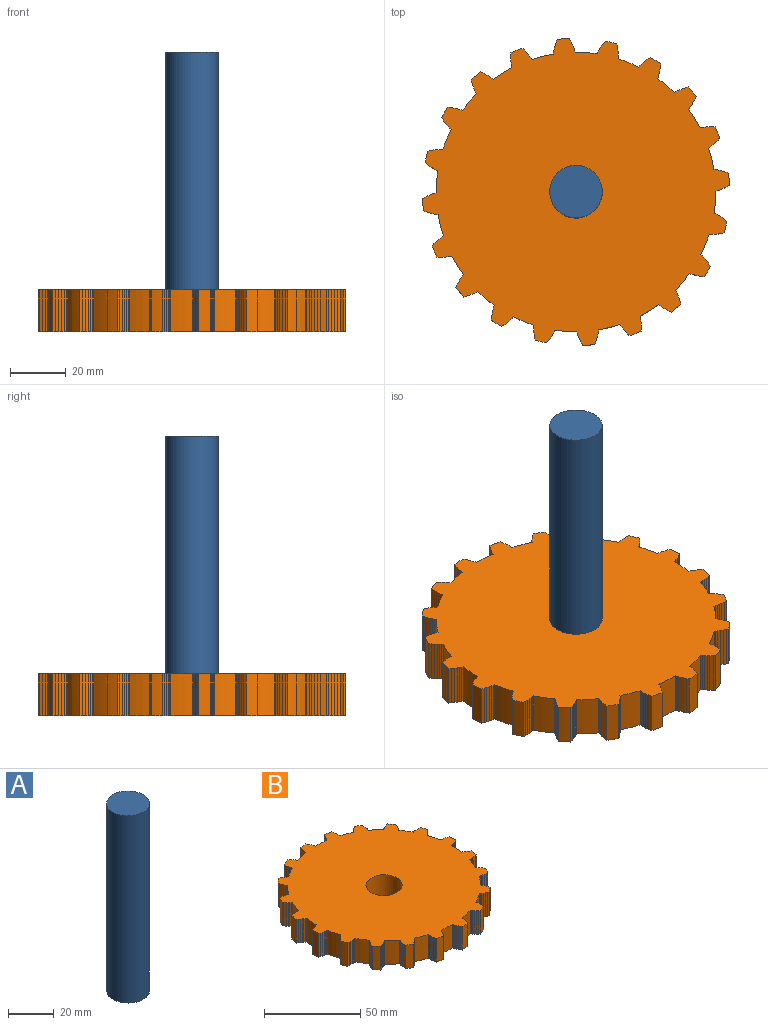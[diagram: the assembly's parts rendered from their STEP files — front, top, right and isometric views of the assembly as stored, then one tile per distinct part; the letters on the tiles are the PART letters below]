
ASSEMBLY  parts=2 mates=1
PART A: 3 faces, bbox 18.8x18.8x100 mm
  f0: cylinder r=9.38mm len=100mm, axis (0,0,-1), area 5890.5mm2, adj f1,f2
  f1: plane 18.75x18.75mm, normal (0,0,1), area 276.1mm2, adj f0
  f2: plane 18.75x18.75mm, normal (0,0,-1), area 276.1mm2, adj f0
PART B: 283 faces, bbox 109.9x109.9x15 mm
  f0: plane 15x0.7mm, normal (-0.45,-0.89,0), area 11.8mm2, adj f1,f279,f281,f282
  f1: plane 15x0.51mm, normal (-0.41,-0.91,0), area 8.4mm2, adj f0,f2,f281,f282
  f2: cylinder r=50mm len=15mm, axis (0,0,-1), area 117.8mm2, adj f1,f3,f281,f282
  f3: plane 15x0.54mm, normal (-0.27,0.96,0), area 8.4mm2, adj f2,f4,f281,f282
  f4: plane 15x0.75mm, normal (-0.32,0.95,0), area 11.8mm2, adj f3,f5,f281,f282
  f5: plane 15x0.84mm, normal (-0.37,0.93,0), area 13.6mm2, adj f4,f6,f281,f282
  f6: plane 15x0.94mm, normal (-0.41,0.91,0), area 15.4mm2, adj f5,f7,f281,f282
  f7: plane 15x1.02mm, normal (-0.46,0.89,0), area 17.2mm2, adj f6,f8,f281,f282
  f8: plane 15x0.86mm, normal (-0.5,0.87,0), area 14.9mm2, adj f7,f9,f281,f282
  f9: cylinder r=55mm len=15mm, axis (0,0,-1), area 64.8mm2, adj f8,f10,f281,f282
  f10: plane 15x0.93mm, normal (-0.35,-0.94,0), area 14.9mm2, adj f9,f11,f281,f282
  f11: plane 15x1.1mm, normal (-0.3,-0.95,0), area 17.2mm2, adj f10,f12,f281,f282
  f12: plane 15x0.99mm, normal (-0.25,-0.97,0), area 15.4mm2, adj f11,f13,f281,f282
  f13: plane 15x0.89mm, normal (-0.21,-0.98,0), area 13.6mm2, adj f12,f14,f281,f282
  f14: plane 15x0.78mm, normal (-0.16,-0.99,0), area 11.8mm2, adj f13,f15,f281,f282
  f15: plane 15x0.56mm, normal (-0.11,-0.99,0), area 8.4mm2, adj f14,f16,f281,f282
  f16: cylinder r=50mm len=15mm, axis (0,0,-1), area 117.8mm2, adj f15,f17,f281,f282
  f17: plane 15x0.46mm, normal (-0.56,0.83,0), area 8.4mm2, adj f16,f18,f281,f282
  f18: plane 15x0.63mm, normal (-0.6,0.8,0), area 11.8mm2, adj f17,f19,f281,f282
  f19: plane 15x0.7mm, normal (-0.64,0.77,0), area 13.6mm2, adj f18,f20,f281,f282
  f20: plane 15x0.76mm, normal (-0.67,0.74,0), area 15.4mm2, adj f19,f21,f281,f282
  f21: plane 15x0.82mm, normal (-0.71,0.7,0), area 17.2mm2, adj f20,f22,f281,f282
  f22: plane 15x0.74mm, normal (-0.74,0.67,0), area 14.9mm2, adj f21,f23,f281,f282
  f23: cylinder r=55mm len=15mm, axis (0,0,-1), area 64.8mm2, adj f22,f24,f281,f282
  f24: plane 15x0.99mm, normal (-0.04,-1,0), area 14.9mm2, adj f23,f25,f281,f282
  f25: plane 15x1.15mm, normal (0.01,-1,0), area 17.2mm2, adj f24,f26,f281,f282
  f26: plane 15x1.03mm, normal (0.06,-1,0), area 15.4mm2, adj f25,f27,f281,f282
  f27: plane 15x0.9mm, normal (0.11,-0.99,0), area 13.6mm2, adj f26,f28,f281,f282
  f28: plane 15x0.78mm, normal (0.16,-0.99,0), area 11.8mm2, adj f27,f29,f281,f282
  f29: plane 15x0.55mm, normal (0.21,-0.98,0), area 8.4mm2, adj f28,f30,f281,f282
  f30: cylinder r=50mm len=15mm, axis (0,0,-1), area 117.8mm2, adj f29,f31,f281,f282
  f31: plane 15x0.44mm, normal (-0.79,0.62,0), area 8.4mm2, adj f30,f32,f281,f282
  f32: plane 15x0.64mm, normal (-0.82,0.58,0), area 11.8mm2, adj f31,f33,f281,f282
  f33: plane 15x0.77mm, normal (-0.84,0.54,0), area 13.6mm2, adj f32,f34,f281,f282
  f34: plane 15x0.89mm, normal (-0.87,0.49,0), area 15.4mm2, adj f33,f35,f281,f282
  f35: plane 15x1.03mm, normal (-0.89,0.45,0), area 17.2mm2, adj f34,f36,f281,f282
  f36: plane 15x0.91mm, normal (-0.91,0.41,0), area 14.9mm2, adj f35,f37,f281,f282
  f37: cylinder r=55mm len=15mm, axis (0,0,-1), area 64.8mm2, adj f36,f38,f281,f282
  f38: plane 15x0.96mm, normal (0.27,-0.96,0), area 14.9mm2, adj f37,f39,f281,f282
  f39: plane 15x1.09mm, normal (0.32,-0.95,0), area 17.2mm2, adj f38,f40,f281,f282
  f40: plane 15x0.96mm, normal (0.36,-0.93,0), area 15.4mm2, adj f39,f41,f281,f282
  f41: plane 15x0.83mm, normal (0.41,-0.91,0), area 13.6mm2, adj f40,f42,f281,f282
  f42: plane 15x0.7mm, normal (0.45,-0.89,0), area 11.8mm2, adj f41,f43,f281,f282
  f43: plane 15x0.48mm, normal (0.5,-0.87,0), area 8.4mm2, adj f42,f44,f281,f282
  f44: cylinder r=50mm len=15mm, axis (0,0,-1), area 117.8mm2, adj f43,f45,f281,f282
  f45: plane 15x0.52mm, normal (-0.94,0.35,0), area 8.4mm2, adj f44,f46,f281,f282
  f46: plane 15x0.75mm, normal (-0.95,0.3,0), area 11.8mm2, adj f45,f47,f281,f282
  f47: plane 15x0.88mm, normal (-0.97,0.25,0), area 13.6mm2, adj f46,f48,f281,f282
  f48: plane 15x1.01mm, normal (-0.98,0.2,0), area 15.4mm2, adj f47,f49,f281,f282
  f49: plane 15x1.14mm, normal (-0.99,0.15,0), area 17.2mm2, adj f48,f50,f281,f282
  f50: plane 15x0.99mm, normal (-0.99,0.1,0), area 14.9mm2, adj f49,f51,f281,f282
  f51: cylinder r=55mm len=15mm, axis (0,0,-1), area 64.8mm2, adj f50,f52,f281,f282
  f52: plane 15x0.83mm, normal (0.55,-0.83,0), area 14.9mm2, adj f51,f53,f281,f282
  f53: plane 15x0.93mm, normal (0.59,-0.8,0), area 17.2mm2, adj f52,f54,f281,f282
  f54: plane 15x0.8mm, normal (0.63,-0.77,0), area 15.4mm2, adj f53,f55,f281,f282
  f55: plane 15x0.67mm, normal (0.67,-0.74,0), area 13.6mm2, adj f54,f56,f281,f282
  f56: plane 15x0.56mm, normal (0.71,-0.71,0), area 11.8mm2, adj f55,f57,f281,f282
  f57: plane 15x0.41mm, normal (0.74,-0.67,0), area 8.4mm2, adj f56,f58,f281,f282
  f58: cylinder r=50mm len=15mm, axis (0,0,-1), area 117.8mm2, adj f57,f59,f281,f282
  f59: plane 15x0.56mm, normal (-1,0.04,0), area 8.4mm2, adj f58,f60,f281,f282
  f60: plane 15x0.79mm, normal (-1,-0.01,0), area 11.8mm2, adj f59,f61,f281,f282
  f61: plane 15x0.91mm, normal (-1,-0.06,0), area 13.6mm2, adj f60,f62,f281,f282
  f62: plane 15x1.02mm, normal (-0.99,-0.11,0), area 15.4mm2, adj f61,f63,f281,f282
  f63: plane 15x1.13mm, normal (-0.99,-0.16,0), area 17.2mm2, adj f62,f64,f281,f282
  f64: plane 15x0.97mm, normal (-0.98,-0.21,0), area 14.9mm2, adj f63,f65,f281,f282
  f65: cylinder r=55mm len=15mm, axis (0,0,-1), area 64.8mm2, adj f64,f66,f281,f282
  f66: plane 15x0.78mm, normal (0.78,-0.62,0), area 14.9mm2, adj f65,f67,f281,f282
  f67: plane 15x0.93mm, normal (0.81,-0.58,0), area 17.2mm2, adj f66,f68,f281,f282
  f68: plane 15x0.87mm, normal (0.84,-0.54,0), area 15.4mm2, adj f67,f69,f281,f282
  f69: plane 15x0.79mm, normal (0.87,-0.5,0), area 13.6mm2, adj f68,f70,f281,f282
  f70: plane 15x0.7mm, normal (0.89,-0.45,0), area 11.8mm2, adj f69,f71,f281,f282
  f71: plane 15x0.51mm, normal (0.91,-0.41,0), area 8.4mm2, adj f70,f72,f281,f282
  f72: cylinder r=50mm len=15mm, axis (0,0,-1), area 117.8mm2, adj f71,f73,f281,f282
  f73: plane 15x0.54mm, normal (-0.96,-0.27,0), area 8.4mm2, adj f72,f74,f281,f282
  f74: plane 15x0.75mm, normal (-0.95,-0.32,0), area 11.8mm2, adj f73,f75,f281,f282
  f75: plane 15x0.84mm, normal (-0.93,-0.37,0), area 13.6mm2, adj f74,f76,f281,f282
  f76: plane 15x0.94mm, normal (-0.91,-0.41,0), area 15.4mm2, adj f75,f77,f281,f282
  f77: plane 15x1.02mm, normal (-0.89,-0.46,0), area 17.2mm2, adj f76,f78,f281,f282
  f78: plane 15x0.86mm, normal (-0.87,-0.5,0), area 14.9mm2, adj f77,f79,f281,f282
  f79: cylinder r=55mm len=15mm, axis (0,0,-1), area 64.8mm2, adj f78,f80,f281,f282
  f80: plane 15x0.93mm, normal (0.94,-0.35,0), area 14.9mm2, adj f79,f81,f281,f282
  f81: plane 15x1.1mm, normal (0.95,-0.3,0), area 17.2mm2, adj f80,f82,f281,f282
  f82: plane 15x0.99mm, normal (0.97,-0.25,0), area 15.4mm2, adj f81,f83,f281,f282
  f83: plane 15x0.89mm, normal (0.98,-0.21,0), area 13.6mm2, adj f82,f84,f281,f282
  f84: plane 15x0.78mm, normal (0.99,-0.16,0), area 11.8mm2, adj f83,f85,f281,f282
  f85: plane 15x0.56mm, normal (0.99,-0.11,0), area 8.4mm2, adj f84,f86,f281,f282
  f86: cylinder r=50mm len=15mm, axis (0,0,-1), area 117.8mm2, adj f85,f87,f281,f282
  f87: plane 15x0.46mm, normal (-0.83,-0.56,0), area 8.4mm2, adj f86,f88,f281,f282
  f88: plane 15x0.63mm, normal (-0.8,-0.6,0), area 11.8mm2, adj f87,f89,f281,f282
  f89: plane 15x0.7mm, normal (-0.77,-0.64,0), area 13.6mm2, adj f88,f90,f281,f282
  f90: plane 15x0.76mm, normal (-0.74,-0.67,0), area 15.4mm2, adj f89,f91,f281,f282
  f91: plane 15x0.82mm, normal (-0.7,-0.71,0), area 17.2mm2, adj f90,f92,f281,f282
  f92: plane 15x0.74mm, normal (-0.67,-0.74,0), area 14.9mm2, adj f91,f93,f281,f282
  f93: cylinder r=55mm len=15mm, axis (0,0,-1), area 64.8mm2, adj f92,f94,f281,f282
  f94: plane 15x0.99mm, normal (1,-0.04,0), area 14.9mm2, adj f93,f95,f281,f282
  f95: plane 15x1.15mm, normal (1,0.01,0), area 17.2mm2, adj f94,f96,f281,f282
  f96: plane 15x1.03mm, normal (1,0.06,0), area 15.4mm2, adj f95,f97,f281,f282
  f97: plane 15x0.9mm, normal (0.99,0.11,0), area 13.6mm2, adj f96,f98,f281,f282
  f98: plane 15x0.78mm, normal (0.99,0.16,0), area 11.8mm2, adj f97,f99,f281,f282
  f99: plane 15x0.55mm, normal (0.98,0.21,0), area 8.4mm2, adj f98,f100,f281,f282
  f100: cylinder r=50mm len=15mm, axis (0,0,-1), area 117.8mm2, adj f99,f101,f281,f282
  f101: plane 15x0.44mm, normal (-0.62,-0.79,0), area 8.4mm2, adj f100,f102,f281,f282
  f102: plane 15x0.64mm, normal (-0.58,-0.82,0), area 11.8mm2, adj f101,f103,f281,f282
  f103: plane 15x0.77mm, normal (-0.54,-0.84,0), area 13.6mm2, adj f102,f104,f281,f282
  f104: plane 15x0.89mm, normal (-0.49,-0.87,0), area 15.4mm2, adj f103,f105,f281,f282
  f105: plane 15x1.03mm, normal (-0.45,-0.89,0), area 17.2mm2, adj f104,f106,f281,f282
  f106: plane 15x0.91mm, normal (-0.41,-0.91,0), area 14.9mm2, adj f105,f107,f281,f282
  f107: cylinder r=55mm len=15mm, axis (0,0,-1), area 64.8mm2, adj f106,f108,f281,f282
  f108: plane 15x0.96mm, normal (0.96,0.27,0), area 14.9mm2, adj f107,f109,f281,f282
  f109: plane 15x1.09mm, normal (0.95,0.32,0), area 17.2mm2, adj f108,f110,f281,f282
  f110: plane 15x0.96mm, normal (0.93,0.36,0), area 15.4mm2, adj f109,f111,f281,f282
  f111: plane 15x0.83mm, normal (0.91,0.41,0), area 13.6mm2, adj f110,f112,f281,f282
  f112: plane 15x0.7mm, normal (0.89,0.45,0), area 11.8mm2, adj f111,f113,f281,f282
  f113: plane 15x0.48mm, normal (0.87,0.5,0), area 8.4mm2, adj f112,f114,f281,f282
  f114: cylinder r=50mm len=15mm, axis (0,0,-1), area 117.8mm2, adj f113,f115,f281,f282
  f115: plane 15x0.52mm, normal (-0.35,-0.94,0), area 8.4mm2, adj f114,f116,f281,f282
  f116: plane 15x0.75mm, normal (-0.3,-0.95,0), area 11.8mm2, adj f115,f117,f281,f282
  f117: plane 15x0.88mm, normal (-0.25,-0.97,0), area 13.6mm2, adj f116,f118,f281,f282
  f118: plane 15x1.01mm, normal (-0.2,-0.98,0), area 15.4mm2, adj f117,f119,f281,f282
  f119: plane 15x1.14mm, normal (-0.15,-0.99,0), area 17.2mm2, adj f118,f120,f281,f282
  f120: plane 15x0.99mm, normal (-0.1,-0.99,0), area 14.9mm2, adj f119,f121,f281,f282
  f121: cylinder r=55mm len=15mm, axis (0,0,-1), area 64.8mm2, adj f120,f122,f281,f282
  f122: plane 15x0.83mm, normal (0.83,0.55,0), area 14.9mm2, adj f121,f123,f281,f282
  f123: plane 15x0.93mm, normal (0.8,0.59,0), area 17.2mm2, adj f122,f124,f281,f282
  f124: plane 15x0.8mm, normal (0.77,0.63,0), area 15.4mm2, adj f123,f125,f281,f282
  f125: plane 15x0.67mm, normal (0.74,0.67,0), area 13.6mm2, adj f124,f126,f281,f282
  f126: plane 15x0.56mm, normal (0.71,0.71,0), area 11.8mm2, adj f125,f127,f281,f282
  f127: plane 15x0.41mm, normal (0.67,0.74,0), area 8.4mm2, adj f126,f128,f281,f282
  f128: cylinder r=50mm len=15mm, axis (0,0,-1), area 117.8mm2, adj f127,f129,f281,f282
  f129: plane 15x0.56mm, normal (-0.04,-1,0), area 8.4mm2, adj f128,f130,f281,f282
  f130: plane 15x0.79mm, normal (0.01,-1,0), area 11.8mm2, adj f129,f131,f281,f282
  f131: plane 15x0.91mm, normal (0.06,-1,0), area 13.6mm2, adj f130,f132,f281,f282
  f132: plane 15x1.02mm, normal (0.11,-0.99,0), area 15.4mm2, adj f131,f133,f281,f282
  f133: plane 15x1.13mm, normal (0.16,-0.99,0), area 17.2mm2, adj f132,f134,f281,f282
  f134: plane 15x0.97mm, normal (0.21,-0.98,0), area 14.9mm2, adj f133,f135,f281,f282
  f135: cylinder r=55mm len=15mm, axis (0,0,-1), area 64.8mm2, adj f134,f136,f281,f282
  f136: plane 15x0.78mm, normal (0.62,0.78,0), area 14.9mm2, adj f135,f137,f281,f282
  f137: plane 15x0.93mm, normal (0.58,0.81,0), area 17.2mm2, adj f136,f138,f281,f282
  f138: plane 15x0.87mm, normal (0.54,0.84,0), area 15.4mm2, adj f137,f139,f281,f282
  f139: plane 15x0.79mm, normal (0.5,0.87,0), area 13.6mm2, adj f138,f140,f281,f282
  f140: plane 15x0.7mm, normal (0.45,0.89,0), area 11.8mm2, adj f139,f141,f281,f282
  f141: plane 15x0.51mm, normal (0.41,0.91,0), area 8.4mm2, adj f140,f142,f281,f282
  f142: cylinder r=50mm len=15mm, axis (0,0,-1), area 117.8mm2, adj f141,f143,f281,f282
  f143: plane 15x0.54mm, normal (0.27,-0.96,0), area 8.4mm2, adj f142,f144,f281,f282
  f144: plane 15x0.75mm, normal (0.32,-0.95,0), area 11.8mm2, adj f143,f145,f281,f282
  f145: plane 15x0.84mm, normal (0.37,-0.93,0), area 13.6mm2, adj f144,f146,f281,f282
  f146: plane 15x0.94mm, normal (0.41,-0.91,0), area 15.4mm2, adj f145,f147,f281,f282
  f147: plane 15x1.02mm, normal (0.46,-0.89,0), area 17.2mm2, adj f146,f148,f281,f282
  f148: plane 15x0.86mm, normal (0.5,-0.87,0), area 14.9mm2, adj f147,f149,f281,f282
  f149: cylinder r=55mm len=15mm, axis (0,0,-1), area 64.8mm2, adj f148,f150,f281,f282
  f150: plane 15x0.93mm, normal (0.35,0.94,0), area 14.9mm2, adj f149,f151,f281,f282
  f151: plane 15x1.1mm, normal (0.3,0.95,0), area 17.2mm2, adj f150,f152,f281,f282
  f152: plane 15x0.99mm, normal (0.25,0.97,0), area 15.4mm2, adj f151,f153,f281,f282
  f153: plane 15x0.89mm, normal (0.21,0.98,0), area 13.6mm2, adj f152,f154,f281,f282
  f154: plane 15x0.78mm, normal (0.16,0.99,0), area 11.8mm2, adj f153,f155,f281,f282
  f155: plane 15x0.56mm, normal (0.11,0.99,0), area 8.4mm2, adj f154,f156,f281,f282
  f156: cylinder r=50mm len=15mm, axis (0,0,-1), area 117.8mm2, adj f155,f157,f281,f282
  f157: plane 15x0.46mm, normal (0.56,-0.83,0), area 8.4mm2, adj f156,f158,f281,f282
  f158: plane 15x0.63mm, normal (0.6,-0.8,0), area 11.8mm2, adj f157,f159,f281,f282
  f159: plane 15x0.7mm, normal (0.64,-0.77,0), area 13.6mm2, adj f158,f160,f281,f282
  f160: plane 15x0.76mm, normal (0.67,-0.74,0), area 15.4mm2, adj f159,f161,f281,f282
  f161: plane 15x0.82mm, normal (0.71,-0.7,0), area 17.2mm2, adj f160,f162,f281,f282
  f162: plane 15x0.74mm, normal (0.74,-0.67,0), area 14.9mm2, adj f161,f163,f281,f282
  f163: cylinder r=55mm len=15mm, axis (0,0,-1), area 64.8mm2, adj f162,f164,f281,f282
  f164: plane 15x0.99mm, normal (0.04,1,0), area 14.9mm2, adj f163,f165,f281,f282
  f165: plane 15x1.15mm, normal (-0.01,1,0), area 17.2mm2, adj f164,f166,f281,f282
  f166: plane 15x1.03mm, normal (-0.06,1,0), area 15.4mm2, adj f165,f167,f281,f282
  f167: plane 15x0.9mm, normal (-0.11,0.99,0), area 13.6mm2, adj f166,f168,f281,f282
  f168: plane 15x0.78mm, normal (-0.16,0.99,0), area 11.8mm2, adj f167,f169,f281,f282
  f169: plane 15x0.55mm, normal (-0.21,0.98,0), area 8.4mm2, adj f168,f170,f281,f282
  f170: cylinder r=50mm len=15mm, axis (0,0,-1), area 117.8mm2, adj f169,f171,f281,f282
  f171: plane 15x0.44mm, normal (0.79,-0.62,0), area 8.4mm2, adj f170,f172,f281,f282
  f172: plane 15x0.64mm, normal (0.82,-0.58,0), area 11.8mm2, adj f171,f173,f281,f282
  f173: plane 15x0.77mm, normal (0.84,-0.54,0), area 13.6mm2, adj f172,f174,f281,f282
  f174: plane 15x0.89mm, normal (0.87,-0.49,0), area 15.4mm2, adj f173,f175,f281,f282
  f175: plane 15x1.03mm, normal (0.89,-0.45,0), area 17.2mm2, adj f174,f176,f281,f282
  f176: plane 15x0.91mm, normal (0.91,-0.41,0), area 14.9mm2, adj f175,f177,f281,f282
  f177: cylinder r=55mm len=15mm, axis (0,0,-1), area 64.8mm2, adj f176,f178,f281,f282
  f178: plane 15x0.96mm, normal (-0.27,0.96,0), area 14.9mm2, adj f177,f179,f281,f282
  f179: plane 15x1.09mm, normal (-0.32,0.95,0), area 17.2mm2, adj f178,f180,f281,f282
  f180: plane 15x0.96mm, normal (-0.36,0.93,0), area 15.4mm2, adj f179,f181,f281,f282
  f181: plane 15x0.83mm, normal (-0.41,0.91,0), area 13.6mm2, adj f180,f182,f281,f282
  f182: plane 15x0.7mm, normal (-0.45,0.89,0), area 11.8mm2, adj f181,f183,f281,f282
  f183: plane 15x0.48mm, normal (-0.5,0.87,0), area 8.4mm2, adj f182,f184,f281,f282
  f184: cylinder r=50mm len=15mm, axis (0,0,-1), area 117.8mm2, adj f183,f185,f281,f282
  f185: plane 15x0.52mm, normal (0.94,-0.35,0), area 8.4mm2, adj f184,f186,f281,f282
  f186: plane 15x0.75mm, normal (0.95,-0.3,0), area 11.8mm2, adj f185,f187,f281,f282
  f187: plane 15x0.88mm, normal (0.97,-0.25,0), area 13.6mm2, adj f186,f188,f281,f282
  f188: plane 15x1.01mm, normal (0.98,-0.2,0), area 15.4mm2, adj f187,f189,f281,f282
  f189: plane 15x1.14mm, normal (0.99,-0.15,0), area 17.2mm2, adj f188,f190,f281,f282
  f190: plane 15x0.99mm, normal (0.99,-0.1,0), area 14.9mm2, adj f189,f191,f281,f282
  f191: cylinder r=55mm len=15mm, axis (0,0,-1), area 64.8mm2, adj f190,f192,f281,f282
  f192: plane 15x0.83mm, normal (-0.55,0.83,0), area 14.9mm2, adj f191,f193,f281,f282
  f193: plane 15x0.93mm, normal (-0.59,0.8,0), area 17.2mm2, adj f192,f194,f281,f282
  f194: plane 15x0.8mm, normal (-0.63,0.77,0), area 15.4mm2, adj f193,f195,f281,f282
  f195: plane 15x0.67mm, normal (-0.67,0.74,0), area 13.6mm2, adj f194,f196,f281,f282
  f196: plane 15x0.56mm, normal (-0.71,0.71,0), area 11.8mm2, adj f195,f197,f281,f282
  f197: plane 15x0.41mm, normal (-0.74,0.67,0), area 8.4mm2, adj f196,f198,f281,f282
  f198: cylinder r=50mm len=15mm, axis (0,0,-1), area 117.8mm2, adj f197,f199,f281,f282
  f199: plane 15x0.56mm, normal (1,-0.04,0), area 8.4mm2, adj f198,f200,f281,f282
  f200: plane 15x0.79mm, normal (1,0.01,0), area 11.8mm2, adj f199,f201,f281,f282
  f201: plane 15x0.91mm, normal (1,0.06,0), area 13.6mm2, adj f200,f202,f281,f282
  f202: plane 15x1.02mm, normal (0.99,0.11,0), area 15.4mm2, adj f201,f203,f281,f282
  f203: plane 15x1.13mm, normal (0.99,0.16,0), area 17.2mm2, adj f202,f204,f281,f282
  f204: plane 15x0.97mm, normal (0.98,0.21,0), area 14.9mm2, adj f203,f205,f281,f282
  f205: cylinder r=55mm len=15mm, axis (0,0,-1), area 64.8mm2, adj f204,f206,f281,f282
  f206: plane 15x0.78mm, normal (-0.78,0.62,0), area 14.9mm2, adj f205,f207,f281,f282
  f207: plane 15x0.93mm, normal (-0.81,0.58,0), area 17.2mm2, adj f206,f208,f281,f282
  f208: plane 15x0.87mm, normal (-0.84,0.54,0), area 15.4mm2, adj f207,f209,f281,f282
  f209: plane 15x0.79mm, normal (-0.87,0.5,0), area 13.6mm2, adj f208,f210,f281,f282
  f210: plane 15x0.7mm, normal (-0.89,0.45,0), area 11.8mm2, adj f209,f211,f281,f282
  f211: plane 15x0.51mm, normal (-0.91,0.41,0), area 8.4mm2, adj f210,f212,f281,f282
  f212: cylinder r=50mm len=15mm, axis (0,0,-1), area 117.8mm2, adj f211,f213,f281,f282
  f213: plane 15x0.54mm, normal (0.96,0.27,0), area 8.4mm2, adj f212,f214,f281,f282
  f214: plane 15x0.75mm, normal (0.95,0.32,0), area 11.8mm2, adj f213,f215,f281,f282
  f215: plane 15x0.84mm, normal (0.93,0.37,0), area 13.6mm2, adj f214,f216,f281,f282
  f216: plane 15x0.94mm, normal (0.91,0.41,0), area 15.4mm2, adj f215,f217,f281,f282
  f217: plane 15x1.02mm, normal (0.89,0.46,0), area 17.2mm2, adj f216,f218,f281,f282
  f218: plane 15x0.86mm, normal (0.87,0.5,0), area 14.9mm2, adj f217,f219,f281,f282
  f219: cylinder r=55mm len=15mm, axis (0,0,-1), area 64.8mm2, adj f218,f220,f281,f282
  f220: plane 15x0.93mm, normal (-0.94,0.35,0), area 14.9mm2, adj f219,f221,f281,f282
  f221: plane 15x1.1mm, normal (-0.95,0.3,0), area 17.2mm2, adj f220,f222,f281,f282
  f222: plane 15x0.99mm, normal (-0.97,0.25,0), area 15.4mm2, adj f221,f223,f281,f282
  f223: plane 15x0.89mm, normal (-0.98,0.21,0), area 13.6mm2, adj f222,f224,f281,f282
  f224: plane 15x0.78mm, normal (-0.99,0.16,0), area 11.8mm2, adj f223,f225,f281,f282
  f225: plane 15x0.56mm, normal (-0.99,0.11,0), area 8.4mm2, adj f224,f226,f281,f282
  f226: cylinder r=50mm len=15mm, axis (0,0,-1), area 117.8mm2, adj f225,f227,f281,f282
  f227: plane 15x0.46mm, normal (0.83,0.56,0), area 8.4mm2, adj f226,f228,f281,f282
  f228: plane 15x0.63mm, normal (0.8,0.6,0), area 11.8mm2, adj f227,f229,f281,f282
  f229: plane 15x0.7mm, normal (0.77,0.64,0), area 13.6mm2, adj f228,f230,f281,f282
  f230: plane 15x0.76mm, normal (0.74,0.67,0), area 15.4mm2, adj f229,f231,f281,f282
  f231: plane 15x0.82mm, normal (0.7,0.71,0), area 17.2mm2, adj f230,f232,f281,f282
  f232: plane 15x0.74mm, normal (0.67,0.74,0), area 14.9mm2, adj f231,f233,f281,f282
  f233: cylinder r=55mm len=15mm, axis (0,0,-1), area 64.8mm2, adj f232,f234,f281,f282
  f234: plane 15x0.99mm, normal (-1,0.04,0), area 14.9mm2, adj f233,f235,f281,f282
  f235: plane 15x1.15mm, normal (-1,-0.01,0), area 17.2mm2, adj f234,f236,f281,f282
  f236: plane 15x1.03mm, normal (-1,-0.06,0), area 15.4mm2, adj f235,f237,f281,f282
  f237: plane 15x0.9mm, normal (-0.99,-0.11,0), area 13.6mm2, adj f236,f238,f281,f282
  f238: plane 15x0.78mm, normal (-0.99,-0.16,0), area 11.8mm2, adj f237,f239,f281,f282
  f239: plane 15x0.55mm, normal (-0.98,-0.21,0), area 8.4mm2, adj f238,f240,f281,f282
  f240: cylinder r=50mm len=15mm, axis (0,0,-1), area 117.8mm2, adj f239,f241,f281,f282
  f241: plane 15x0.44mm, normal (0.62,0.79,0), area 8.4mm2, adj f240,f242,f281,f282
  f242: plane 15x0.64mm, normal (0.58,0.82,0), area 11.8mm2, adj f241,f243,f281,f282
  f243: plane 15x0.77mm, normal (0.54,0.84,0), area 13.6mm2, adj f242,f244,f281,f282
  f244: plane 15x0.89mm, normal (0.49,0.87,0), area 15.4mm2, adj f243,f245,f281,f282
  f245: plane 15x1.03mm, normal (0.45,0.89,0), area 17.2mm2, adj f244,f246,f281,f282
  f246: plane 15x0.91mm, normal (0.41,0.91,0), area 14.9mm2, adj f245,f247,f281,f282
  f247: cylinder r=55mm len=15mm, axis (0,0,-1), area 64.8mm2, adj f246,f248,f281,f282
  f248: plane 15x0.96mm, normal (-0.96,-0.27,0), area 14.9mm2, adj f247,f249,f281,f282
  f249: plane 15x1.09mm, normal (-0.95,-0.32,0), area 17.2mm2, adj f248,f250,f281,f282
  f250: plane 15x0.96mm, normal (-0.93,-0.36,0), area 15.4mm2, adj f249,f251,f281,f282
  f251: plane 15x0.83mm, normal (-0.91,-0.41,0), area 13.6mm2, adj f250,f252,f281,f282
  f252: plane 15x0.7mm, normal (-0.89,-0.45,0), area 11.8mm2, adj f251,f253,f281,f282
  f253: plane 15x0.48mm, normal (-0.87,-0.5,0), area 8.4mm2, adj f252,f254,f281,f282
  f254: cylinder r=50mm len=15mm, axis (0,0,-1), area 117.8mm2, adj f253,f255,f281,f282
  f255: plane 15x0.52mm, normal (0.35,0.94,0), area 8.4mm2, adj f254,f256,f281,f282
  f256: plane 15x0.75mm, normal (0.3,0.95,0), area 11.8mm2, adj f255,f257,f281,f282
  f257: plane 15x0.88mm, normal (0.25,0.97,0), area 13.6mm2, adj f256,f258,f281,f282
  f258: plane 15x1.01mm, normal (0.2,0.98,0), area 15.4mm2, adj f257,f259,f281,f282
  f259: plane 15x1.14mm, normal (0.15,0.99,0), area 17.2mm2, adj f258,f260,f281,f282
  f260: plane 15x0.99mm, normal (0.1,0.99,0), area 14.9mm2, adj f259,f261,f281,f282
  f261: cylinder r=55mm len=15mm, axis (0,0,-1), area 64.8mm2, adj f260,f262,f281,f282
  f262: plane 15x0.83mm, normal (-0.83,-0.55,0), area 14.9mm2, adj f261,f263,f281,f282
  f263: plane 15x0.93mm, normal (-0.8,-0.59,0), area 17.2mm2, adj f262,f264,f281,f282
  f264: plane 15x0.8mm, normal (-0.77,-0.63,0), area 15.4mm2, adj f263,f265,f281,f282
  f265: plane 15x0.67mm, normal (-0.74,-0.67,0), area 13.6mm2, adj f264,f266,f281,f282
  f266: plane 15x0.56mm, normal (-0.71,-0.71,0), area 11.8mm2, adj f265,f267,f281,f282
  f267: plane 15x0.41mm, normal (-0.67,-0.74,0), area 8.4mm2, adj f266,f268,f281,f282
  f268: cylinder r=50mm len=15mm, axis (0,0,-1), area 117.8mm2, adj f267,f269,f281,f282
  f269: plane 15x0.56mm, normal (0.04,1,0), area 8.4mm2, adj f268,f270,f281,f282
  f270: plane 15x0.79mm, normal (-0.01,1,0), area 11.8mm2, adj f269,f271,f281,f282
  f271: plane 15x0.91mm, normal (-0.06,1,0), area 13.6mm2, adj f270,f272,f281,f282
  f272: plane 15x1.02mm, normal (-0.11,0.99,0), area 15.4mm2, adj f271,f273,f281,f282
  f273: plane 15x1.13mm, normal (-0.16,0.99,0), area 17.2mm2, adj f272,f274,f281,f282
  f274: plane 15x0.97mm, normal (-0.21,0.98,0), area 14.9mm2, adj f273,f275,f281,f282
  f275: cylinder r=55mm len=15mm, axis (0,0,-1), area 64.8mm2, adj f274,f276,f281,f282
  f276: plane 15x0.78mm, normal (-0.62,-0.78,0), area 14.9mm2, adj f275,f277,f281,f282
  f277: plane 15x0.93mm, normal (-0.58,-0.81,0), area 17.2mm2, adj f276,f278,f281,f282
  f278: plane 15x0.87mm, normal (-0.54,-0.84,0), area 15.4mm2, adj f277,f279,f281,f282
  f279: plane 15x0.79mm, normal (-0.5,-0.87,0), area 13.6mm2, adj f0,f278,f281,f282
  f280: cylinder r=9.38mm len=18.75mm, axis (0,0,-1), area 883.6mm2, adj f281,f282
  f281: plane 109.89x109.89mm, normal (0,0,1), area 8212.8mm2, adj f0,f1,f2,f3,f4,f5,f6,f7
  f282: plane 109.89x109.89mm, normal (0,0,-1), area 8212.8mm2, adj f0,f1,f2,f3,f4,f5,f6,f7
PLACE A t=(0,0,-19.9)mm
PLACE B t=(0,0,-19.9)mm
MATE cylindrical B.f280 <-> A.f0  axis (0,0,-1) through (0,0,-19.9)mm
